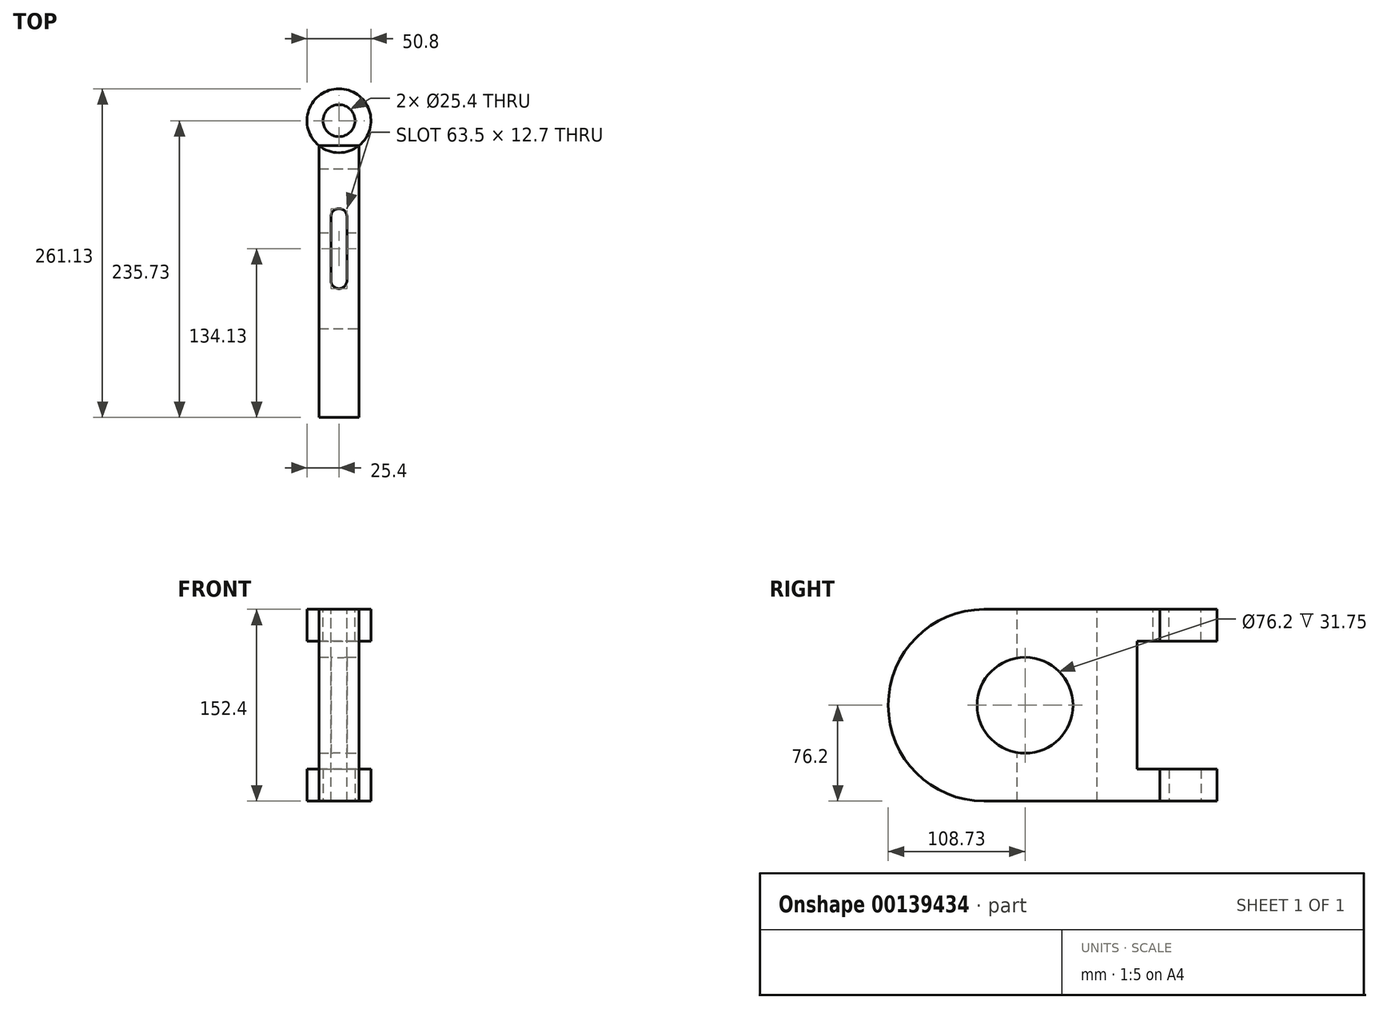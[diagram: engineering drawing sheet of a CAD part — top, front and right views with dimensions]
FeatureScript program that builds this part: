
annotation { "Feature Type Name" : "Feature", "Feature Type Description" : "" }
export const myFeature = defineFeature(function(context is Context, id is Id, definition is map)
    precondition{}
    {
        {
            var Q0;
            Q0=qCreatedBy(makeId("Top.planeOp"),FACE);
            var sketch = newSketch(context, id + "F0", { "sketchPlane" : qUnion([Q0])});
            skLineSegment(sketch, "E0", {"start": v(0, 0) * mm, "end": v(0, -63.5) * mm});
            skArc(sketch, "E1", {"start": v(6.35, -63.5) * mm, "mid": v(0, -57.15) * mm, "end": v(-6.35, -63.5) * mm});
            skLineSegment(sketch, "E2", {"start": v(6.35, -63.5) * mm, "end": v(6.35, -114.3) * mm});
            skLineSegment(sketch, "E3", {"start": v(0, 0) * mm, "end": v(0, 12.7) * mm});
            skCircle(sketch, "E4", {"center": v(0, 12.7) * mm, "radius": 12.7 * mm});
            skCircle(sketch, "E5", {"center": v(0, 12.7) * mm, "radius": 25.4 * mm});
            skPoint(sketch, "E6", {"position": v(15.87, -7.13) * mm});
            skPoint(sketch, "E7", {"position": v(-15.87, -7.13) * mm});
            skLineSegment(sketch, "E8.bottom", {"start": v(-15.87, -7.13) * mm, "end": v(15.88, -7.13) * mm});
            skLineSegment(sketch, "E8.top", {"start": v(-15.87, -146.83) * mm, "end": v(15.87, -146.83) * mm});
            skLineSegment(sketch, "E8.left", {"start": v(-15.87, -7.13) * mm, "end": v(-15.87, -146.83) * mm});
            skLineSegment(sketch, "E8.right", {"start": v(15.87, -7.13) * mm, "end": v(15.88, -146.83) * mm});
            skLineSegment(sketch, "E9", {"start": v(0, -63.5) * mm, "end": v(0, -114.3) * mm});
            skLineSegment(sketch, "E10", {"start": v(-6.35, -63.5) * mm, "end": v(-6.35, -114.3) * mm});
            skArc(sketch, "E11", {"start": v(-6.35, -114.3) * mm, "mid": v(0, -120.65) * mm, "end": v(6.35, -114.3) * mm});
            skLineSegment(sketch, "E12", {"start": v(0, 12.7) * mm, "end": v(0, -29.81) * mm});
            skSolve(sketch);
        }
        {
            var Q0;
            {var subQ4=sQuery(id+"F0.wireOp",EDGE,"E2");Q0=makeQuery(id+"F0.imprint","IMPRINT",FACE,{"disambiguationData":[TD([[makeQuery(id+"F0.imprint","IMPRINT",EDGE,{"derivedFrom":subQ4}),1.0]])]});}
            var Q1;
            {var subQ1=sQuery(id+"F0.wireOp",EDGE,"E5");var subQ3=sQuery(id+"F0.wireOp",EDGE,"E12");var subQ4=makeQuery(id+"F0.imprint","INTERSECT",VERTEX,{"derivedFrom":[subQ1,subQ3]});Q1=makeQuery(id+"F0.imprint","IMPRINT",FACE,{"disambiguationData":[TD([[makeQuery(id+"F0.imprint","IMPRINT",EDGE,{"disambiguationData":[TD([[subQ4,1.0]])],"derivedFrom":subQ3}),1.0]])]});}
            var Q2;
            {var subQ1=sQuery(id+"F0.wireOp",EDGE,"E5");var subQ3=sQuery(id+"F0.wireOp",EDGE,"E12");var subQ4=makeQuery(id+"F0.imprint","INTERSECT",VERTEX,{"derivedFrom":[subQ1,subQ3]});Q2=makeQuery(id+"F0.imprint","IMPRINT",FACE,{"disambiguationData":[TD([[makeQuery(id+"F0.imprint","IMPRINT",EDGE,{"disambiguationData":[TD([[subQ4,1.0]])],"derivedFrom":subQ3}),-1.0]])]});}
            extrude(context, id + "F1", {"entities" : qUnion([Q0, Q1, Q2]), "oppositeDirection" : true, "depth" : 152.4 * mm});
        }
        {
            var Q0;
            Q0=makeQuery(id+"F0.imprint","IMPRINT",FACE,{"disambiguationData":[TD([[makeQuery(id+"F0.imprint","IMPRINT",EDGE,{"derivedFrom":sQuery(id+"F0.wireOp",EDGE,"E4")}),-1.0]])]});
            extrude(context, id + "F2", {"entities" : qUnion([Q0]), "operationType" : NewBodyOperationType.ADD, "oppositeDirection" : true, "depth" : 25.4 * mm});
        }
        {
            var Q0;
            Q0=makeQuery(id+"F1.opExtrude","SWEPT_FACE",FACE,{"disambiguationData":[OSD([sQuery(id+"F0.wireOp",EDGE,"E8.right")])]});
            var sketch = newSketch(context, id + "F3", { "sketchPlane" : qUnion([Q0])});
            skLineSegment(sketch, "E13", {"start": v(0, 0) * mm, "end": v(-25.4, 0) * mm});
            skLineSegment(sketch, "E14", {"start": v(-25.4, 0) * mm, "end": v(-114.3, 0) * mm});
            skLineSegment(sketch, "E15", {"start": v(-7.13, -25.4) * mm, "end": v(-7.13, -127) * mm});
            skCircle(sketch, "E16", {"center": v(-114.3, -76.2) * mm, "radius": 38.1 * mm});
            skPoint(sketch, "E16.centerSnap0", {"position": v(-7.13, -76.2) * mm});
            skArc(sketch, "E17", {"start": v(-146.83, 0) * mm, "mid": v(-223.03, -76.2) * mm, "end": v(-146.83, -152.4) * mm});
            skLineSegment(sketch, "E18", {"start": v(-7.13, -25.4) * mm, "end": v(-25.4, -25.4) * mm});
            skLineSegment(sketch, "E19", {"start": v(-25.4, -25.4) * mm, "end": v(-25.4, -127) * mm});
            skLineSegment(sketch, "E20", {"start": v(-25.4, -127) * mm, "end": v(-7.13, -127) * mm});
            skSolve(sketch);
        }
        {
            var Q0;
            {var subQ5=sQuery(id+"F3.wireOp",EDGE,"E17");Q0=makeQuery(id+"F3.imprint","IMPRINT",FACE,{"disambiguationData":[TD([[makeQuery(id+"F3.imprint","IMPRINT",EDGE,{"derivedFrom":subQ5}),1.0]])]});}
            extrude(context, id + "F4", {"entities" : qUnion([Q0]), "operationType" : NewBodyOperationType.ADD, "oppositeDirection" : true, "depth" : 31.75 * mm});
        }
        {
            var Q0;
            {var subQ0=sQuery(id+"F3.wireOp",EDGE,"E16");var subQ1=makeQuery(id+"F1.opExtrude","SWEPT_EDGE",EDGE,{"disambiguationData":[OSD([sQuery(id+"F0.wireOp",EDGE,"E8.top"),sQuery(id+"F0.wireOp",EDGE,"E8.right")])]});var subQ2=makeQuery(id+"F3.imprint","INTERSECT",VERTEX,{"disambiguationData":[OD(0.0)],"derivedFrom":[subQ1,subQ0]});Q0=makeQuery(id+"F3.imprint","IMPRINT",FACE,{"disambiguationData":[TD([[makeQuery(id+"F3.imprint","IMPRINT",EDGE,{"disambiguationData":[TD([[subQ2,1.0]])],"derivedFrom":subQ0}),1.0]])]});}
            extrude(context, id + "F5", {"entities" : qUnion([Q0]), "operationType" : NewBodyOperationType.REMOVE, "endBound" : BoundingType.THROUGH_ALL, "oppositeDirection" : true, "depth" : 25.4 * mm});
        }
        {
            var Q0;
            Q0=makeQuery(id+"F3.imprint","IMPRINT",FACE,{"disambiguationData":[TD([[makeQuery(id+"F3.imprint","IMPRINT",EDGE,{"derivedFrom":sQuery(id+"F3.wireOp",EDGE,"E15")}),1.0]])]});
            extrude(context, id + "F6", {"entities" : qUnion([Q0]), "operationType" : NewBodyOperationType.REMOVE, "endBound" : BoundingType.THROUGH_ALL, "oppositeDirection" : true, "depth" : 25.4 * mm});
        }
        {
            var Q0;
            Q0=makeQuery(id+"F1.opExtrude","CAP_FACE",FACE,{"disambiguationData":[OSD([sQuery(id+"F0.wireOp",EDGE,"E1"),sQuery(id+"F0.wireOp",EDGE,"E2"),sQuery(id+"F0.wireOp",EDGE,"E8.bottom"),sQuery(id+"F0.wireOp",EDGE,"E8.top"),sQuery(id+"F0.wireOp",EDGE,"E8.left"),sQuery(id+"F0.wireOp",EDGE,"E8.right"),sQuery(id+"F0.wireOp",EDGE,"E10"),sQuery(id+"F0.wireOp",EDGE,"E11")])],"isStart":false});
            var sketch = newSketch(context, id + "F7", { "sketchPlane" : qUnion([Q0])});
            skLineSegment(sketch, "E21", {"start": v(0, 0) * mm, "end": v(0, -12.7) * mm});
            skCircle(sketch, "E22", {"center": v(0, -12.7) * mm, "radius": 12.7 * mm});
            skCircle(sketch, "E23", {"center": v(0, -12.7) * mm, "radius": 25.4 * mm});
            skSolve(sketch);
        }
        {
            var Q0;
            Q0=makeQuery(id+"F7.imprint","IMPRINT",FACE,{"disambiguationData":[TD([[makeQuery(id+"F7.imprint","IMPRINT",EDGE,{"derivedFrom":sQuery(id+"F7.wireOp",EDGE,"E22")}),-1.0]])]});
            extrude(context, id + "F8", {"entities" : qUnion([Q0]), "operationType" : NewBodyOperationType.ADD, "oppositeDirection" : true, "depth" : 25.4 * mm});
        }
    });
